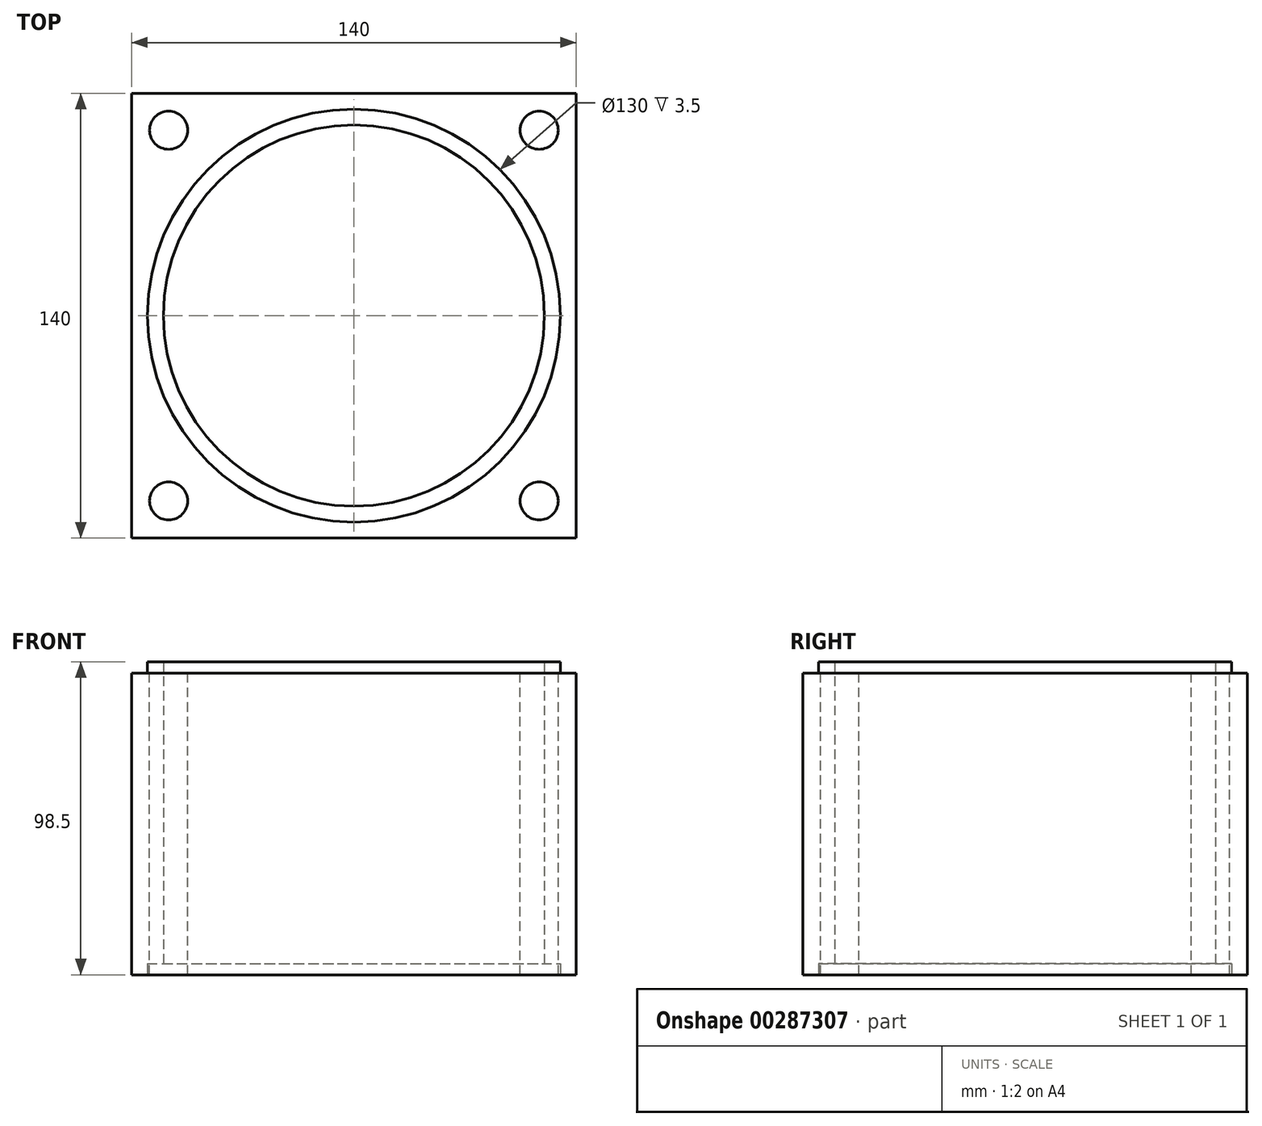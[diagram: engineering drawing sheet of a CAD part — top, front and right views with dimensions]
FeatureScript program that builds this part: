
annotation { "Feature Type Name" : "Feature", "Feature Type Description" : "" }
export const myFeature = defineFeature(function(context is Context, id is Id, definition is map)
    precondition{}
    {
        {
            var Q0;
            Q0=qCreatedBy(makeId("Top.planeOp"),FACE);
            var sketch = newSketch(context, id + "F0", { "sketchPlane" : qUnion([Q0])});
            skLineSegment(sketch, "E0.bottom", {"start": v(-70, 70) * mm, "end": v(70, 70) * mm});
            skLineSegment(sketch, "E0.top", {"start": v(-70, -70) * mm, "end": v(70, -70) * mm});
            skLineSegment(sketch, "E0.left", {"start": v(-70, 70) * mm, "end": v(-70, -70) * mm});
            skLineSegment(sketch, "E0.right", {"start": v(70, 70) * mm, "end": v(70, -70) * mm});
            skCircle(sketch, "E1", {"center": v(0, 0) * mm, "radius": 60 * mm});
            skSolve(sketch);
        }
        {
            var Q0;
            Q0 = qSketchRegion(id + "F0", true);
            extrude(context, id + "F1", {"entities" : qUnion([Q0]), "depth" : 95 * mm});
        }
        {
            var Q0;
            Q0=makeQuery(id+"F1.opExtrude","CAP_FACE",FACE,{"disambiguationData":[OSD([sQuery(id+"F0.wireOp",EDGE,"E0.bottom"),sQuery(id+"F0.wireOp",EDGE,"E0.top"),sQuery(id+"F0.wireOp",EDGE,"E0.left"),sQuery(id+"F0.wireOp",EDGE,"E0.right"),sQuery(id+"F0.wireOp",EDGE,"E1")])],"isStart":false});
            var sketch = newSketch(context, id + "F2", { "sketchPlane" : qUnion([Q0])});
            skCircle(sketch, "E2", {"center": v(0, 0) * mm, "radius": 65 * mm});
            skCircle(sketch, "E3", {"center": v(0, 0) * mm, "radius": 60 * mm});
            skSolve(sketch);
        }
        {
            var Q0;
            Q0 = qSketchRegion(id + "F2", true);
            extrude(context, id + "F3", {"entities" : qUnion([Q0]), "operationType" : NewBodyOperationType.ADD, "depth" : 3.5 * mm});
        }
        {
            var Q0;
            Q0=makeQuery(id+"F1.opExtrude","CAP_FACE",FACE,{"disambiguationData":[OSD([sQuery(id+"F0.wireOp",EDGE,"E0.bottom"),sQuery(id+"F0.wireOp",EDGE,"E0.top"),sQuery(id+"F0.wireOp",EDGE,"E0.left"),sQuery(id+"F0.wireOp",EDGE,"E0.right"),sQuery(id+"F0.wireOp",EDGE,"E1")])],"isStart":true});
            var sketch = newSketch(context, id + "F4", { "sketchPlane" : qUnion([Q0])});
            skCircle(sketch, "E4", {"center": v(0, 0) * mm, "radius": 65 * mm});
            skCircle(sketch, "E5", {"center": v(0, 0) * mm, "radius": 50 * mm});
            skSolve(sketch);
        }
        {
            var Q0;
            Q0 = qSketchRegion(id + "F4", true);
            extrude(context, id + "F5", {"entities" : qUnion([Q0]), "operationType" : NewBodyOperationType.REMOVE, "oppositeDirection" : true, "depth" : 3.5 * mm});
        }
        {
            var Q0;
            Q0=makeQuery(id+"F1.opExtrude","CAP_FACE",FACE,{"disambiguationData":[OSD([sQuery(id+"F0.wireOp",EDGE,"E0.bottom"),sQuery(id+"F0.wireOp",EDGE,"E0.top"),sQuery(id+"F0.wireOp",EDGE,"E0.left"),sQuery(id+"F0.wireOp",EDGE,"E0.right"),sQuery(id+"F0.wireOp",EDGE,"E1")])],"isStart":false});
            var sketch = newSketch(context, id + "F6", { "sketchPlane" : qUnion([Q0])});
            skCircle(sketch, "E6", {"center": v(0, 0) * mm, "radius": 82.5 * mm});
            skLineSegment(sketch, "E7", {"start": v(0, 0) * mm, "end": v(-70, 70) * mm});
            skCircle(sketch, "E8", {"center": v(-58.34, 58.34) * mm, "radius": 6 * mm});
            skCircle(sketch, "E9.1.0", {"center": v(-58.34, -58.34) * mm, "radius": 6 * mm});
            skCircle(sketch, "E9.2.0", {"center": v(58.34, -58.34) * mm, "radius": 6 * mm});
            skCircle(sketch, "E9.3.0", {"center": v(58.34, 58.34) * mm, "radius": 6 * mm});
            skLineSegment(sketch, "E9.anchor1", {"start": v(0, 0) * mm, "end": v(-58.34, 58.34) * mm, "construction": true});
            skLineSegment(sketch, "E9.anchor2", {"start": v(0, 0) * mm, "end": v(58.34, 58.34) * mm, "construction": true});
            skSolve(sketch);
        }
        {
            var Q0;
            {var subQ0=sQuery(id+"F6.wireOp",EDGE,"E8");var subQ1=sQuery(id+"F6.wireOp",EDGE,"E6");var subQ2=makeQuery(id+"F6.imprint","INTERSECT",VERTEX,{"disambiguationData":[OD(0.0)],"derivedFrom":[subQ1,subQ0]});Q0=makeQuery(id+"F6.imprint","IMPRINT",FACE,{"disambiguationData":[TD([[makeQuery(id+"F6.imprint","IMPRINT",EDGE,{"disambiguationData":[TD([[subQ2,-1.0]])],"derivedFrom":subQ1}),-1.0]])]});}
            var Q1;
            {var subQ0=sQuery(id+"F6.wireOp",EDGE,"E8");var subQ1=sQuery(id+"F6.wireOp",EDGE,"E6");var subQ2=makeQuery(id+"F6.imprint","INTERSECT",VERTEX,{"disambiguationData":[OD(0.0)],"derivedFrom":[subQ1,subQ0]});Q1=makeQuery(id+"F6.imprint","IMPRINT",FACE,{"disambiguationData":[TD([[makeQuery(id+"F6.imprint","IMPRINT",EDGE,{"disambiguationData":[TD([[subQ2,-1.0]])],"derivedFrom":subQ1}),1.0]])]});}
            var Q2;
            {var subQ0=sQuery(id+"F6.wireOp",EDGE,"E7");var subQ1=sQuery(id+"F6.wireOp",EDGE,"E6");var subQ2=makeQuery(id+"F6.imprint","INTERSECT",VERTEX,{"derivedFrom":[subQ1,subQ0]});Q2=makeQuery(id+"F6.imprint","IMPRINT",FACE,{"disambiguationData":[TD([[makeQuery(id+"F6.imprint","IMPRINT",EDGE,{"disambiguationData":[TD([[subQ2,-1.0]])],"derivedFrom":subQ1}),1.0]])]});}
            var Q3;
            {var subQ0=sQuery(id+"F6.wireOp",EDGE,"E7");var subQ1=sQuery(id+"F6.wireOp",EDGE,"E6");var subQ2=makeQuery(id+"F6.imprint","INTERSECT",VERTEX,{"derivedFrom":[subQ1,subQ0]});Q3=makeQuery(id+"F6.imprint","IMPRINT",FACE,{"disambiguationData":[TD([[makeQuery(id+"F6.imprint","IMPRINT",EDGE,{"disambiguationData":[TD([[subQ2,-1.0]])],"derivedFrom":subQ1}),-1.0]])]});}
            var Q4;
            {var subQ0=sQuery(id+"F6.wireOp",EDGE,"E9.3.0");var subQ1=sQuery(id+"F6.wireOp",EDGE,"E6");var subQ2=makeQuery(id+"F6.imprint","INTERSECT",VERTEX,{"disambiguationData":[OD(0.0)],"derivedFrom":[subQ1,subQ0]});Q4=makeQuery(id+"F6.imprint","IMPRINT",FACE,{"disambiguationData":[TD([[makeQuery(id+"F6.imprint","IMPRINT",EDGE,{"disambiguationData":[TD([[subQ2,-1.0]])],"derivedFrom":subQ1}),-1.0]])]});}
            var Q5;
            {var subQ0=sQuery(id+"F6.wireOp",EDGE,"E9.3.0");var subQ1=sQuery(id+"F6.wireOp",EDGE,"E6");var subQ2=makeQuery(id+"F6.imprint","INTERSECT",VERTEX,{"disambiguationData":[OD(0.0)],"derivedFrom":[subQ1,subQ0]});Q5=makeQuery(id+"F6.imprint","IMPRINT",FACE,{"disambiguationData":[TD([[makeQuery(id+"F6.imprint","IMPRINT",EDGE,{"disambiguationData":[TD([[subQ2,-1.0]])],"derivedFrom":subQ1}),1.0]])]});}
            var Q6;
            {var subQ0=sQuery(id+"F6.wireOp",EDGE,"E9.2.0");var subQ1=sQuery(id+"F6.wireOp",EDGE,"E6");var subQ2=makeQuery(id+"F6.imprint","INTERSECT",VERTEX,{"disambiguationData":[OD(0.0)],"derivedFrom":[subQ1,subQ0]});Q6=makeQuery(id+"F6.imprint","IMPRINT",FACE,{"disambiguationData":[TD([[makeQuery(id+"F6.imprint","IMPRINT",EDGE,{"disambiguationData":[TD([[subQ2,-1.0]])],"derivedFrom":subQ1}),-1.0]])]});}
            var Q7;
            {var subQ0=sQuery(id+"F6.wireOp",EDGE,"E9.2.0");var subQ1=sQuery(id+"F6.wireOp",EDGE,"E6");var subQ2=makeQuery(id+"F6.imprint","INTERSECT",VERTEX,{"disambiguationData":[OD(0.0)],"derivedFrom":[subQ1,subQ0]});Q7=makeQuery(id+"F6.imprint","IMPRINT",FACE,{"disambiguationData":[TD([[makeQuery(id+"F6.imprint","IMPRINT",EDGE,{"disambiguationData":[TD([[subQ2,-1.0]])],"derivedFrom":subQ1}),1.0]])]});}
            var Q8;
            {var subQ0=sQuery(id+"F6.wireOp",EDGE,"E9.1.0");var subQ1=sQuery(id+"F6.wireOp",EDGE,"E6");var subQ2=makeQuery(id+"F6.imprint","INTERSECT",VERTEX,{"disambiguationData":[OD(0.0)],"derivedFrom":[subQ1,subQ0]});Q8=makeQuery(id+"F6.imprint","IMPRINT",FACE,{"disambiguationData":[TD([[makeQuery(id+"F6.imprint","IMPRINT",EDGE,{"disambiguationData":[TD([[subQ2,-1.0]])],"derivedFrom":subQ1}),-1.0]])]});}
            var Q9;
            {var subQ0=sQuery(id+"F6.wireOp",EDGE,"E9.1.0");var subQ1=sQuery(id+"F6.wireOp",EDGE,"E6");var subQ2=makeQuery(id+"F6.imprint","INTERSECT",VERTEX,{"disambiguationData":[OD(0.0)],"derivedFrom":[subQ1,subQ0]});Q9=makeQuery(id+"F6.imprint","IMPRINT",FACE,{"disambiguationData":[TD([[makeQuery(id+"F6.imprint","IMPRINT",EDGE,{"disambiguationData":[TD([[subQ2,-1.0]])],"derivedFrom":subQ1}),1.0]])]});}
            extrude(context, id + "F7", {"entities" : qUnion([Q0, Q1, Q2, Q3, Q4, Q5, Q6, Q7, Q8, Q9]), "operationType" : NewBodyOperationType.REMOVE, "endBound" : BoundingType.THROUGH_ALL, "oppositeDirection" : true, "depth" : 25 * mm});
        }
    });
